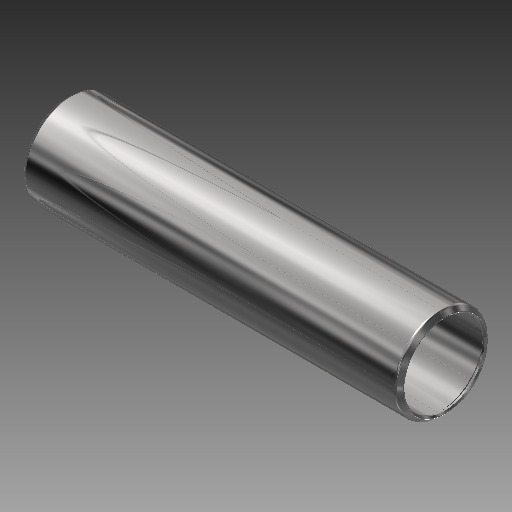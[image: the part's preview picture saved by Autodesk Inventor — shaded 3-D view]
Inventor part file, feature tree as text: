
AUTODESK INVENTOR PART (.ipt)
format: ipt  version: 2017 (Build 210142000, 142)  size: 209,920 bytes
history: native  units: in
note: dims shown in document units (in); Inventor stores cm internally (conversion verified against a paired STEP export)
features: other x42, revolve x1, sketch x1
ambient origin geometry x8: Origin, YZ Plane, XZ Plane, XY Plane, X Axis, Y Axis, Z Axis, Center Point
bodies: Solid1 (feature_tree)
feature tree (44):
  revolve  "Revolution1"  [1 undecoded]
  other  "cp1_XY"
  other  "cp1_YZ"
  other  "cp1_ZX"
  other  "cp1_X"
  other  "cp1_Y"
  other  "cp1_Z"
  other  "cp1_Center"
  other  "cp2_XY"
  other  "cp2_YZ"
  other  "cp2_ZX"
  other  "cp2_X"
  other  "cp2_Y"
  other  "cp2_Z"
  other  "cp2_Center"
  other  "cp3_XY"
  other  "cp3_YZ"
  other  "cp3_ZX"
  other  "cp3_X"
  other  "cp3_Y"
  other  "cp3_Z"
  other  "cp3_Center"
  other  "cp4_XY"
  other  "cp4_YZ"
  other  "cp4_ZX"
  other  "cp4_X"
  other  "cp4_Y"
  other  "cp4_Z"
  other  "cp4_Center"
  other  "tube_front_XY"
  other  "tube_front_YZ"
  other  "tube_front_ZX"
  other  "tube_front_X"
  other  "tube_front_Y"
  other  "tube_front_Z"
  other  "tube_front_Center"
  other  "tube_rear_XY"
  other  "tube_rear_YZ"
  other  "tube_rear_ZX"
  other  "tube_rear_X"
  other  "tube_rear_Y"
  other  "tube_rear_Z"
  other  "tube_rear_Center"
  sketch  "Sketch_1"  dims[d0=360.0deg]
note: 1 required parameter value undecoded (feature->parameter linkage not recoverable at this tier; creation-order binding heuristic only, values carry confidence <= 0.55)
